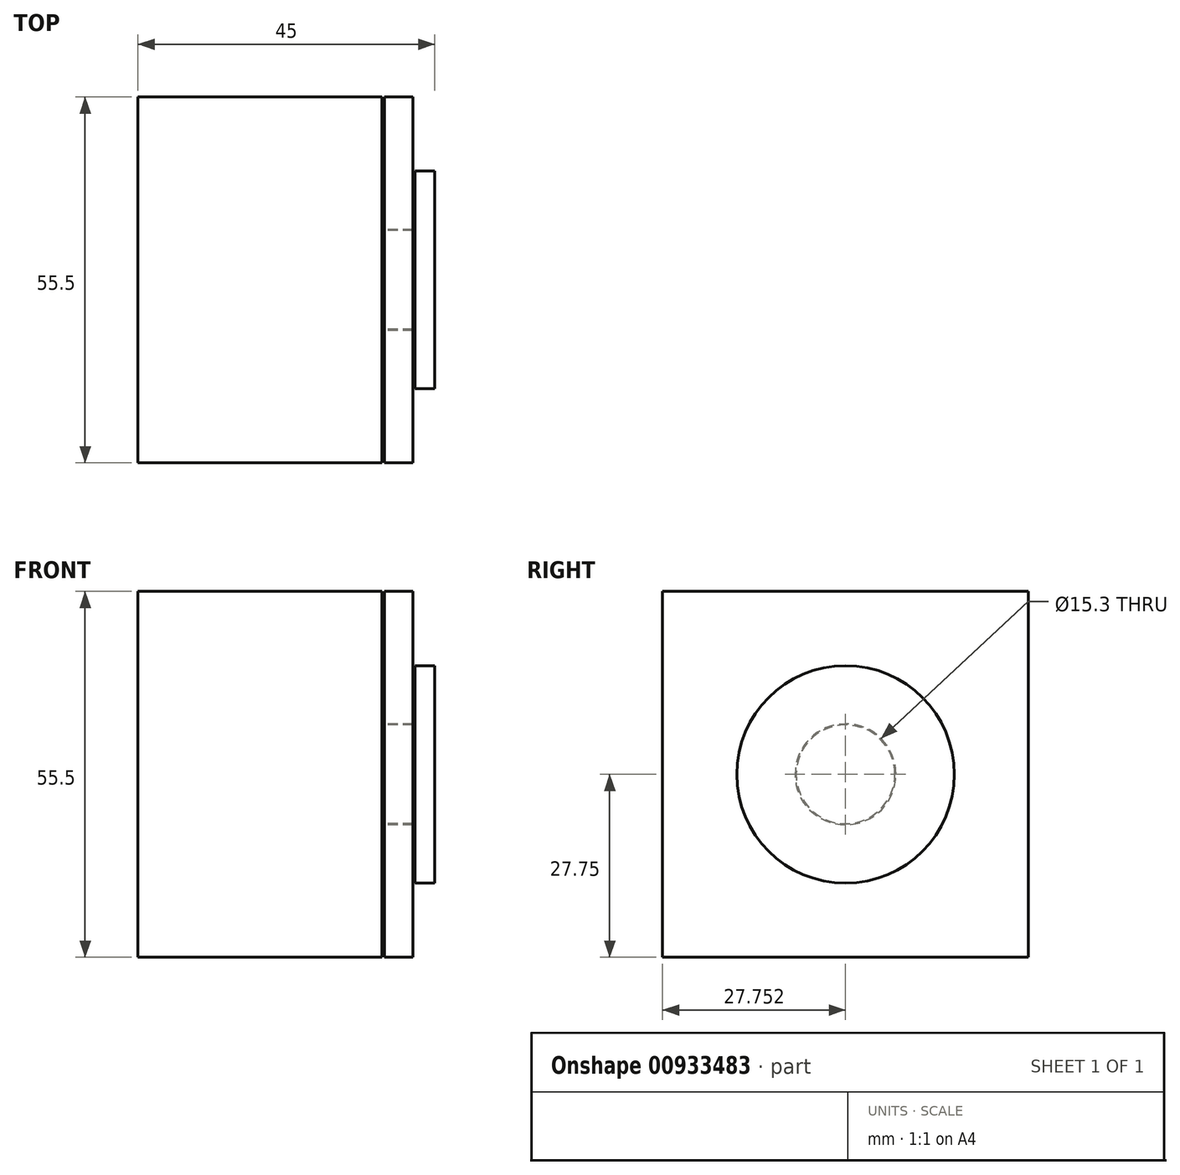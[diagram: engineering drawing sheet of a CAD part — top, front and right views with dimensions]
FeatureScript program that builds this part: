
annotation { "Feature Type Name" : "Feature", "Feature Type Description" : "" }
export const myFeature = defineFeature(function(context is Context, id is Id, definition is map)
    precondition{}
    {
        {
            var Q0;
            Q0=qCreatedBy(makeId("Right.planeOp"),FACE);
            var sketch = newSketch(context, id + "F0", { "sketchPlane" : qUnion([Q0])});
            skLineSegment(sketch, "E0.bottom", {"start": v(-15.52, 55.5) * mm, "end": v(39.98, 55.5) * mm});
            skLineSegment(sketch, "E0.top", {"start": v(-15.52, 0) * mm, "end": v(39.98, 0) * mm});
            skLineSegment(sketch, "E0.left", {"start": v(-15.52, 55.5) * mm, "end": v(-15.52, 0) * mm});
            skLineSegment(sketch, "E0.right", {"start": v(39.98, 55.5) * mm, "end": v(39.98, 0) * mm});
            skCircle(sketch, "E1", {"center": v(12.23, 27.75) * mm, "radius": 7.5 * mm});
            skSolve(sketch);
        }
        {
            var Q0;
            Q0=makeQuery(id+"F0.imprint","IMPRINT",FACE,{"disambiguationData":[TD([[makeQuery(id+"F0.imprint","IMPRINT",EDGE,{"derivedFrom":sQuery(id+"F0.wireOp",EDGE,"E1")}),1.0]])]});
            var Q1;
            Q1=makeQuery(id+"F0.imprint","IMPRINT",FACE,{"disambiguationData":[TD([[makeQuery(id+"F0.imprint","IMPRINT",EDGE,{"derivedFrom":sQuery(id+"F0.wireOp",EDGE,"E0.bottom")}),-1.0]])]});
            extrude(context, id + "F1", {"entities" : qUnion([Q0, Q1]), "oppositeDirection" : true, "depth" : 37 * mm, "offsetDistance" : 25 * mm});
        }
        {
            var Q0;
            Q0=makeQuery(id+"F0.imprint","IMPRINT",FACE,{"disambiguationData":[TD([[makeQuery(id+"F0.imprint","IMPRINT",EDGE,{"derivedFrom":sQuery(id+"F0.wireOp",EDGE,"E1")}),1.0]])]});
            extrude(context, id + "F2", {"entities" : qUnion([Q0]), "operationType" : NewBodyOperationType.ADD, "depth" : 5 * mm, "offsetDistance" : 25 * mm});
        }
        {
            var Q0;
            Q0=makeQuery(id+"F2.opExtrude","CAP_FACE",FACE,{"disambiguationData":[OSD([sQuery(id+"F0.wireOp",EDGE,"E1")])],"isStart":false});
            var sketch = newSketch(context, id + "F3", { "sketchPlane" : qUnion([Q0])});
            skCircle(sketch, "E2", {"center": v(12.23, 27.75) * mm, "radius": 16.5 * mm});
            skSolve(sketch);
        }
        {
            var Q0;
            Q0=makeQuery(id+"F3.imprint","IMPRINT",FACE,{"disambiguationData":[TD([[makeQuery(id+"F3.imprint","IMPRINT",EDGE,{"derivedFrom":sQuery(id+"F3.wireOp",EDGE,"E2")}),1.0]])]});
            var Q1;
            Q1=makeQuery(id+"F3.imprint","IMPRINT",FACE,{"disambiguationData":[TD([[makeQuery(id+"F3.imprint","IMPRINT",EDGE,{"derivedFrom":makeQuery(id+"F2.opExtrude","CAP_EDGE",EDGE,{"disambiguationData":[OSD([sQuery(id+"F0.wireOp",EDGE,"E1")])],"isStart":false})}),1.0]])]});
            extrude(context, id + "F4", {"entities" : qUnion([Q0, Q1]), "operationType" : NewBodyOperationType.ADD, "depth" : 3 * mm, "offsetDistance" : 25 * mm});
        }
        {
            var Q0;
            Q0=makeQuery(id+"F0.imprint","IMPRINT",FACE,{"disambiguationData":[TD([[makeQuery(id+"F0.imprint","IMPRINT",EDGE,{"derivedFrom":sQuery(id+"F0.wireOp",EDGE,"E0.bottom")}),-1.0]])]});
            cPlane(context, id + "F5", {"entities" : qUnion([Q0]), "cplaneType" : CPlaneType.OFFSET, "offset" : 0.4 * mm, "width" : 150 * mm, "height" : 150 * mm});
        }
        {
            var Q0;
            Q0=qCreatedBy(id+"F5.planeOp",FACE);
            var sketch = newSketch(context, id + "F6", { "sketchPlane" : qUnion([Q0])});
            skLineSegment(sketch, "E3.bottom", {"start": v(-15.52, 55.5) * mm, "end": v(39.98, 55.5) * mm});
            skLineSegment(sketch, "E3.top", {"start": v(-15.52, 0) * mm, "end": v(39.98, 0) * mm});
            skLineSegment(sketch, "E3.left", {"start": v(-15.52, 55.5) * mm, "end": v(-15.52, 0) * mm});
            skLineSegment(sketch, "E3.right", {"start": v(39.98, 55.5) * mm, "end": v(39.98, 0) * mm});
            skCircle(sketch, "E4", {"center": v(12.23, 27.75) * mm, "radius": 7.65 * mm});
            skSolve(sketch);
        }
        {
            var Q0;
            Q0=makeQuery(id+"F6.imprint","IMPRINT",FACE,{"disambiguationData":[TD([[makeQuery(id+"F6.imprint","IMPRINT",EDGE,{"derivedFrom":sQuery(id+"F6.wireOp",EDGE,"E3.bottom")}),-1.0]])]});
            extrude(context, id + "F7", {"entities" : qUnion([Q0]), "depth" : 4.3 * mm, "offsetDistance" : 25 * mm});
        }
    });
